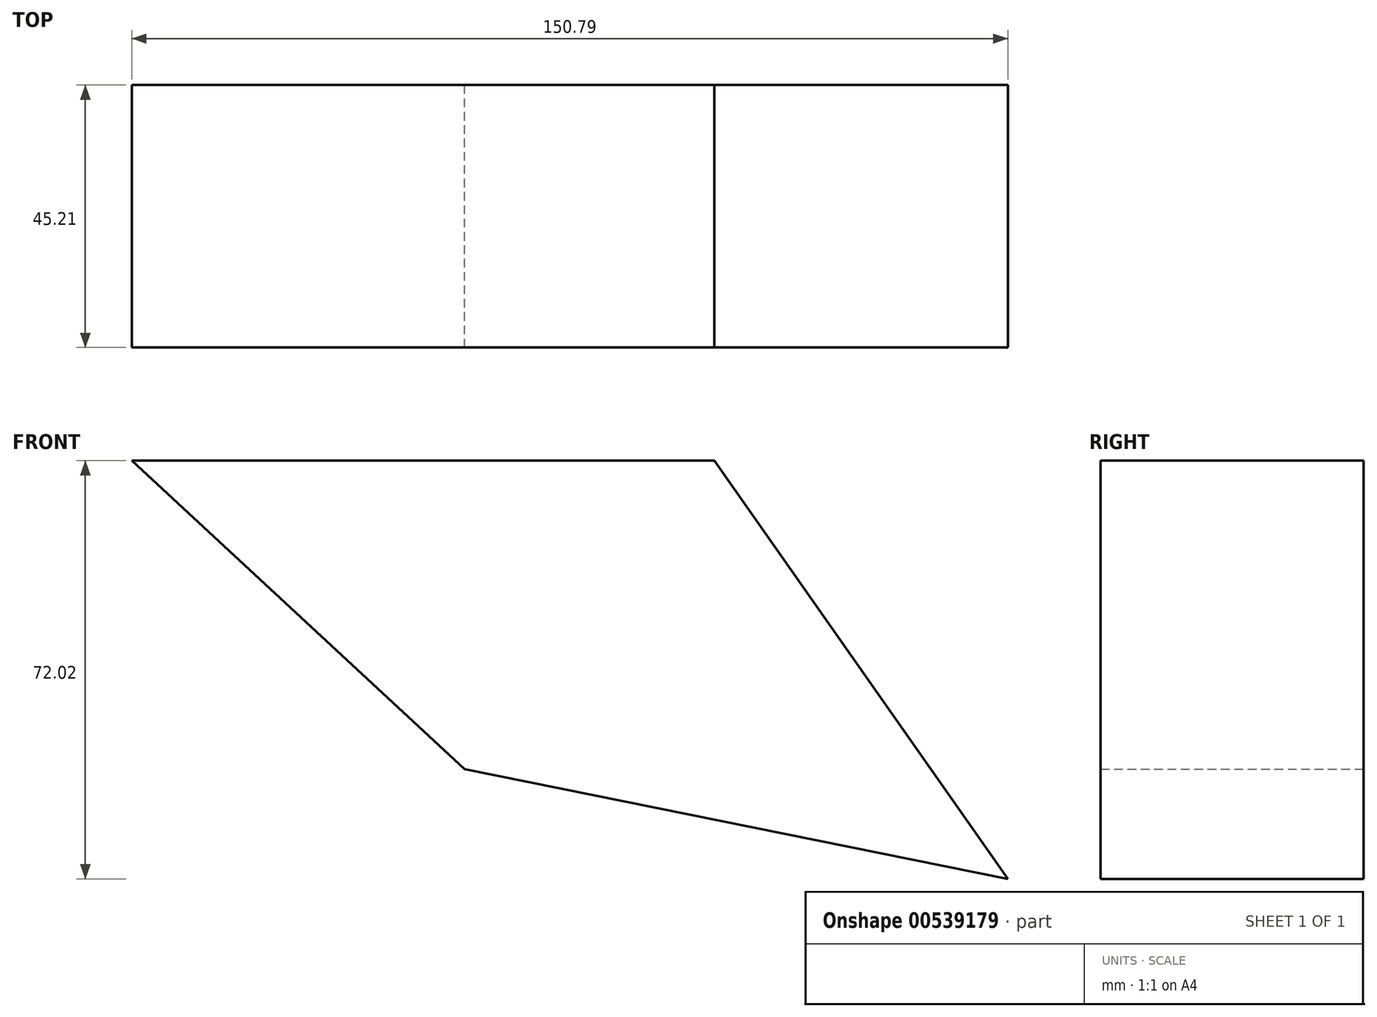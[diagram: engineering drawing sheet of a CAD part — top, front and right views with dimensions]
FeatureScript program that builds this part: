
annotation { "Feature Type Name" : "Feature", "Feature Type Description" : "" }
export const myFeature = defineFeature(function(context is Context, id is Id, definition is map)
    precondition{}
    {
        {
            var Q0;
            Q0=qCreatedBy(makeId("Front.planeOp"),FACE);
            var sketch = newSketch(context, id + "F0", { "sketchPlane" : qUnion([Q0])});
            skLineSegment(sketch, "E0", {"start": v(0, 0) * mm, "end": v(-57.3, 53.12) * mm});
            skLineSegment(sketch, "E1", {"start": v(-57.3, 53.12) * mm, "end": v(42.97, 53.12) * mm});
            skLineSegment(sketch, "E2", {"start": v(42.97, 53.12) * mm, "end": v(93.5, -18.9) * mm});
            skLineSegment(sketch, "E3", {"start": v(93.5, -18.9) * mm, "end": v(0, 0) * mm});
            skSolve(sketch);
        }
        {
            var Q0;
            Q0=makeQuery(id+"F0.imprint","IMPRINT",FACE,{"disambiguationData":[TD([[makeQuery(id+"F0.imprint","IMPRINT",EDGE,{"derivedFrom":sQuery(id+"F0.wireOp",EDGE,"E0")}),-1.0]])]});
            extrude(context, id + "F1", {"entities" : qUnion([Q0]), "depth" : 45.2 * mm, "offsetDistance" : 25.4 * mm});
        }
    });
